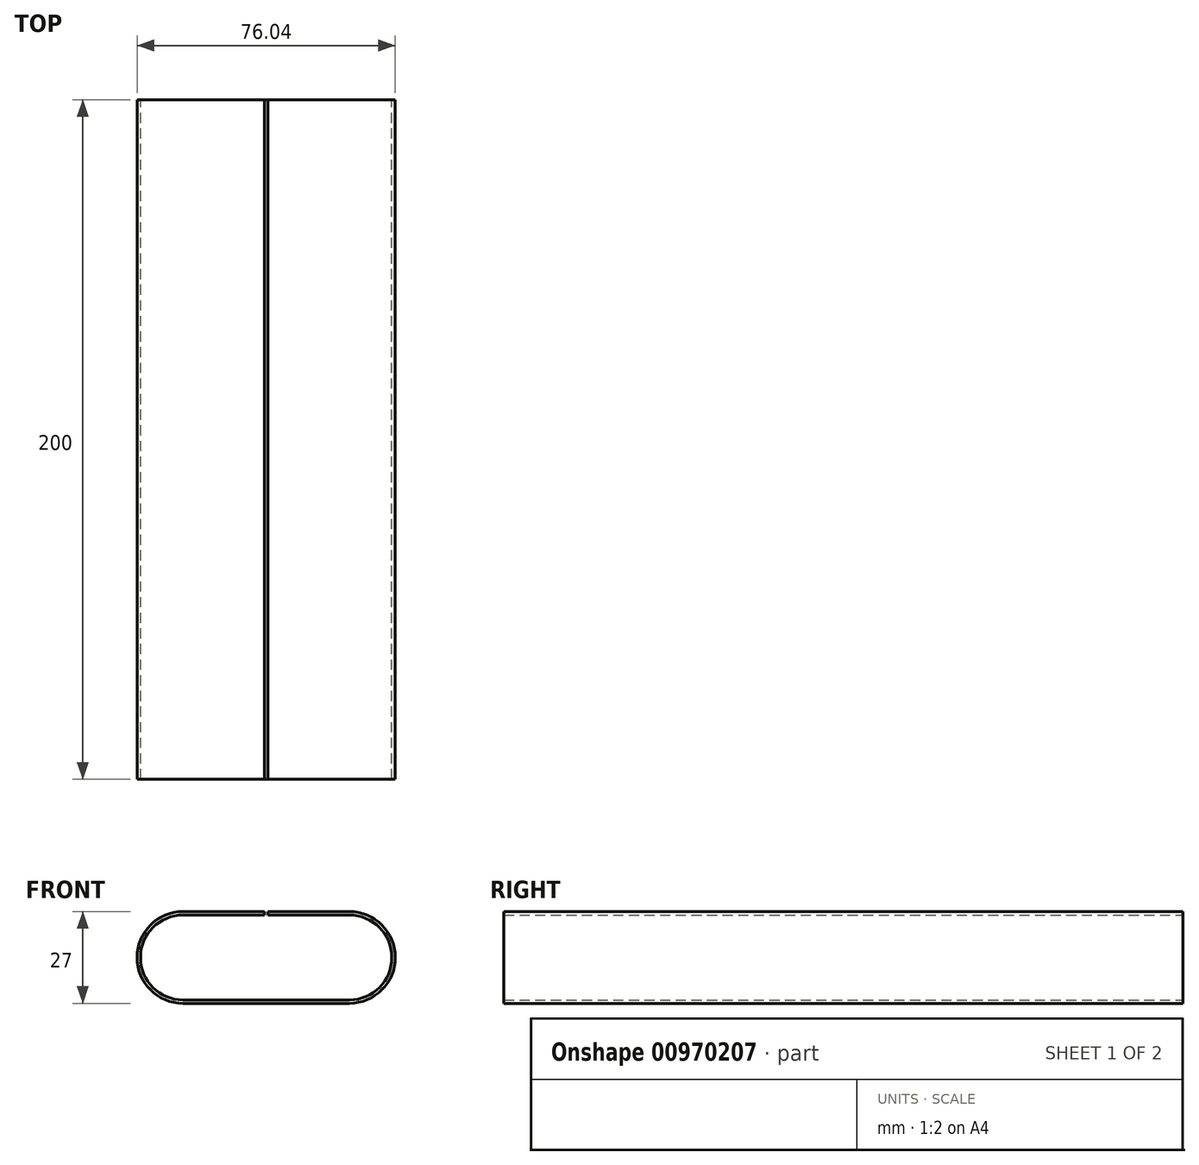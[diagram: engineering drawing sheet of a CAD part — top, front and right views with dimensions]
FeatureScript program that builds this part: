
annotation { "Feature Type Name" : "Feature", "Feature Type Description" : "" }
export const myFeature = defineFeature(function(context is Context, id is Id, definition is map)
    precondition{}
    {
        {
            var Q0;
            Q0=qCreatedBy(makeId("Front.planeOp"),FACE);
            var sketch = newSketch(context, id + "F0", { "sketchPlane" : qUnion([Q0])});
            skLineSegment(sketch, "E0.bottom", {"start": v(-28.4, 43.23) * mm, "end": v(20.65, 43.23) * mm});
            skLineSegment(sketch, "E0.top", {"start": v(-28.4, 70.23) * mm, "end": v(-4.37, 70.23) * mm});
            skArc(sketch, "E1", {"start": v(-28.4, 70.23) * mm, "mid": v(-41.9, 56.73) * mm, "end": v(-28.4, 43.23) * mm});
            skArc(sketch, "E2", {"start": v(20.65, 43.23) * mm, "mid": v(34.15, 56.73) * mm, "end": v(20.65, 70.23) * mm});
            skLineSegment(sketch, "E3.0", {"start": v(-28.4, 44.23) * mm, "end": v(20.65, 44.23) * mm});
            skArc(sketch, "E3.1", {"start": v(-28.4, 69.23) * mm, "mid": v(-40.9, 56.73) * mm, "end": v(-28.4, 44.23) * mm});
            skLineSegment(sketch, "E3.2", {"start": v(-28.4, 69.23) * mm, "end": v(-4.37, 69.23) * mm});
            skArc(sketch, "E3.3", {"start": v(20.65, 44.23) * mm, "mid": v(33.15, 56.73) * mm, "end": v(20.65, 69.23) * mm});
            skLineSegment(sketch, "E4", {"start": v(-3.37, 70.23) * mm, "end": v(-3.37, 69.23) * mm});
            skLineSegment(sketch, "E5", {"start": v(-4.37, 70.23) * mm, "end": v(-4.37, 69.23) * mm});
            skLineSegment(sketch, "E6", {"start": v(-3.37, 69.23) * mm, "end": v(20.65, 69.23) * mm});
            skLineSegment(sketch, "E7", {"start": v(-3.37, 70.23) * mm, "end": v(20.65, 70.23) * mm});
            skLineSegment(sketch, "E8", {"start": v(-4.37, 69.23) * mm, "end": v(-4.37, 69.23) * mm});
            skSolve(sketch);
        }
        {
            var Q0;
            Q0 = qSketchRegion(id + "F0", true);
            extrude(context, id + "F1", {"entities" : qUnion([Q0]), "depth" : 200 * mm, "offsetDistance" : 25 * mm});
        }
    });
